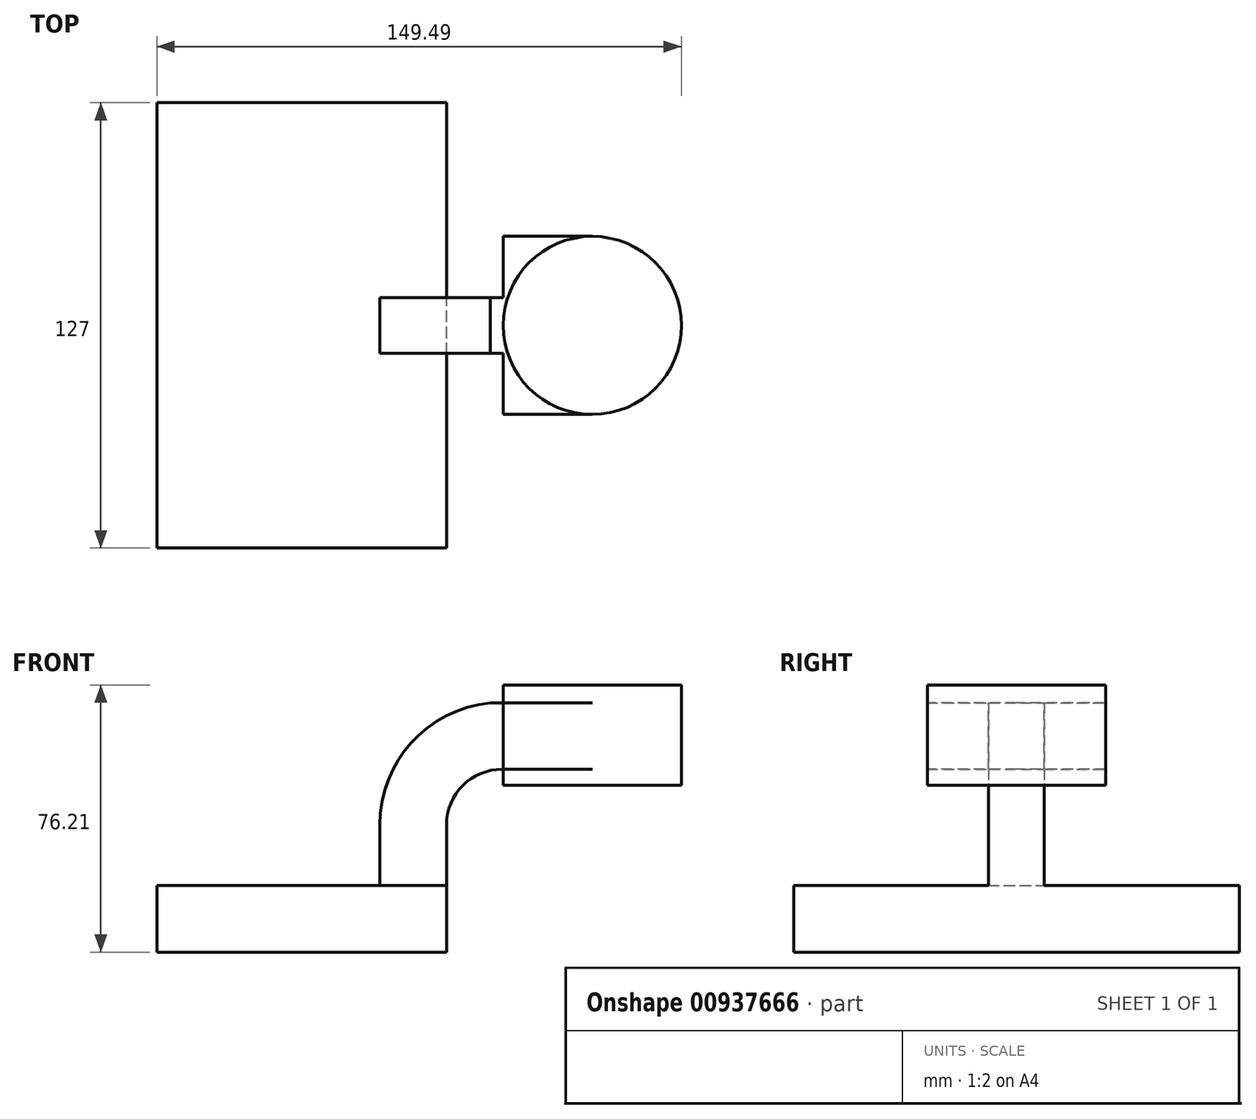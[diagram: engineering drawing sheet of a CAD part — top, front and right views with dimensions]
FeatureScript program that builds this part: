
annotation { "Feature Type Name" : "Feature", "Feature Type Description" : "" }
export const myFeature = defineFeature(function(context is Context, id is Id, definition is map)
    precondition{}
    {
        {
            var Q0;
            Q0=qCreatedBy(makeId("Front.planeOp"),FACE);
            var sketch = newSketch(context, id + "F0", { "sketchPlane" : qUnion([Q0])});
            skLineSegment(sketch, "E0.bottom", {"start": v(-75.98, 9.53) * mm, "end": v(6.57, 9.53) * mm});
            skLineSegment(sketch, "E0.top", {"start": v(-75.98, -9.52) * mm, "end": v(6.57, -9.52) * mm});
            skLineSegment(sketch, "E0.left", {"start": v(-75.98, 9.52) * mm, "end": v(-75.98, -9.53) * mm});
            skLineSegment(sketch, "E0.right", {"start": v(6.57, 9.52) * mm, "end": v(6.57, -9.53) * mm});
            skPoint(sketch, "E0.middle", {"position": v(-34.7, 0) * mm});
            skPoint(sketch, "E1.middle", {"position": v(6.57, 9.52) * mm});
            skLineSegment(sketch, "E2.bottom", {"start": v(-5.74, 9.53) * mm, "end": v(-9.17, 9.53) * mm});
            skLineSegment(sketch, "E2.top", {"start": v(-5.74, 9.53) * mm, "end": v(-9.17, 9.53) * mm});
            skLineSegment(sketch, "E2.left", {"start": v(-5.74, 9.53) * mm, "end": v(-5.74, 9.53) * mm});
            skLineSegment(sketch, "E2.right", {"start": v(-9.17, 9.53) * mm, "end": v(-9.17, 9.53) * mm});
            skPoint(sketch, "E2.middle", {"position": v(-7.45, 9.53) * mm});
            skLineSegment(sketch, "E3", {"start": v(6.57, 9.52) * mm, "end": v(6.57, 9.52) * mm});
            skPoint(sketch, "E4.middle", {"position": v(48.11, 94.8) * mm});
            skLineSegment(sketch, "E5.bottom", {"start": v(73.51, 38.1) * mm, "end": v(22.71, 38.1) * mm});
            skLineSegment(sketch, "E5.top", {"start": v(73.51, 66.68) * mm, "end": v(22.71, 66.68) * mm});
            skLineSegment(sketch, "E5.left", {"start": v(73.51, 38.1) * mm, "end": v(73.51, 66.67) * mm});
            skLineSegment(sketch, "E5.right", {"start": v(22.71, 38.1) * mm, "end": v(22.71, 66.67) * mm});
            skPoint(sketch, "E5.middle", {"position": v(48.11, 52.39) * mm});
            skLineSegment(sketch, "E6", {"start": v(6.57, 9.52) * mm, "end": v(6.57, 26.75) * mm});
            skArc(sketch, "E7", {"start": v(6.57, 26.75) * mm, "mid": v(11.22, 37.97) * mm, "end": v(22.45, 42.62) * mm});
            skLineSegment(sketch, "E8", {"start": v(22.45, 42.62) * mm, "end": v(48.11, 42.62) * mm});
            skArc(sketch, "E9.0", {"start": v(-12.48, 26.75) * mm, "mid": v(-3.44, 50.19) * mm, "end": v(18.99, 61.5) * mm});
            skLineSegment(sketch, "E9.1", {"start": v(-12.48, 9.53) * mm, "end": v(-12.48, 26.75) * mm});
            skLineSegment(sketch, "E10", {"start": v(18.99, 61.5) * mm, "end": v(48.11, 61.5) * mm});
            skLineSegment(sketch, "E11", {"start": v(48.11, 52.39) * mm, "end": v(48.11, 66.68) * mm});
            skLineSegment(sketch, "E12", {"start": v(48.11, 52.39) * mm, "end": v(48.11, 38.1) * mm});
            skLineSegment(sketch, "E13", {"start": v(48.11, 38.1) * mm, "end": v(48.11, 66.68) * mm});
            skFitSpline(sketch, "E14", {"points": [v(-75.98, 9.52) * mm, v(-57.73, 37.05) * mm, v(-32.15, 59.03) * mm, v(18.99, 61.5) * mm], "startDerivative": vector(138.7, 155.83) * mm, "endDerivative": vector(128.85, -24.49) * mm});
            skSolve(sketch);
        }
        {
            var Q0;
            Q0=makeQuery(id+"F0.imprint","IMPRINT",FACE,{"disambiguationData":[TD([[makeQuery(id+"F0.imprint","IMPRINT",EDGE,{"derivedFrom":sQuery(id+"F0.wireOp",EDGE,"E0.top")}),1.0]])]});
            extrude(context, id + "F1", {"entities" : qUnion([Q0]), "endBound" : BoundingType.SYMMETRIC, "depth" : 127 * mm, "offsetDistance" : 25.4 * mm});
        }
        {
            var Q0;
            {var subQ7=sQuery(id+"F0.wireOp",EDGE,"E2.top");Q0=makeQuery(id+"F0.imprint","IMPRINT",FACE,{"disambiguationData":[TD([[makeQuery(id+"F0.imprint","IMPRINT",EDGE,{"derivedFrom":subQ7}),-1.0]])]});}
            var Q1;
            {var subQ0=sQuery(id+"F0.wireOp",EDGE,"E8");var subQ1=sQuery(id+"F0.wireOp",EDGE,"E5.right");var subQ2=makeQuery(id+"F0.imprint","INTERSECT",VERTEX,{"derivedFrom":[subQ1,subQ0]});Q1=makeQuery(id+"F0.imprint","IMPRINT",FACE,{"disambiguationData":[TD([[makeQuery(id+"F0.imprint","IMPRINT",EDGE,{"disambiguationData":[TD([[subQ2,-1.0]])],"derivedFrom":subQ1}),-1.0]])]});}
            extrude(context, id + "F2", {"entities" : qUnion([Q0, Q1]), "operationType" : NewBodyOperationType.ADD, "endBound" : BoundingType.SYMMETRIC, "depth" : 50.8 * mm, "offsetDistance" : 25.4 * mm});
        }
        {
            var Q0;
            Q0=makeQuery(id+"F0.imprint","IMPRINT",FACE,{"disambiguationData":[TD([[makeQuery(id+"F0.imprint","IMPRINT",EDGE,{"derivedFrom":sQuery(id+"F0.wireOp",EDGE,"E9.0")}),1.0]])]});
            extrude(context, id + "F3", {"entities" : qUnion([Q0]), "operationType" : NewBodyOperationType.ADD, "endBound" : BoundingType.SYMMETRIC, "depth" : 15.88 * mm, "offsetDistance" : 25.4 * mm});
        }
        {
            var Q0;
            {var subQ4=sQuery(id+"F0.wireOp",EDGE,"E5.left");Q0=makeQuery(id+"F0.imprint","IMPRINT",FACE,{"disambiguationData":[TD([[makeQuery(id+"F0.imprint","IMPRINT",EDGE,{"derivedFrom":subQ4}),1.0]])]});}
            var Q1;
            Q1=sQuery(id+"F0.wireOp",EDGE,"E11");
            revolve(context, id + "F4", {"operationType" : NewBodyOperationType.ADD, "surfaceOperationType" : NewSurfaceOperationType.NEW, "entities" : qUnion([Q0]), "axis" : qUnion([Q1]), "revolveType" : RevolveType.FULL});
        }
    });
